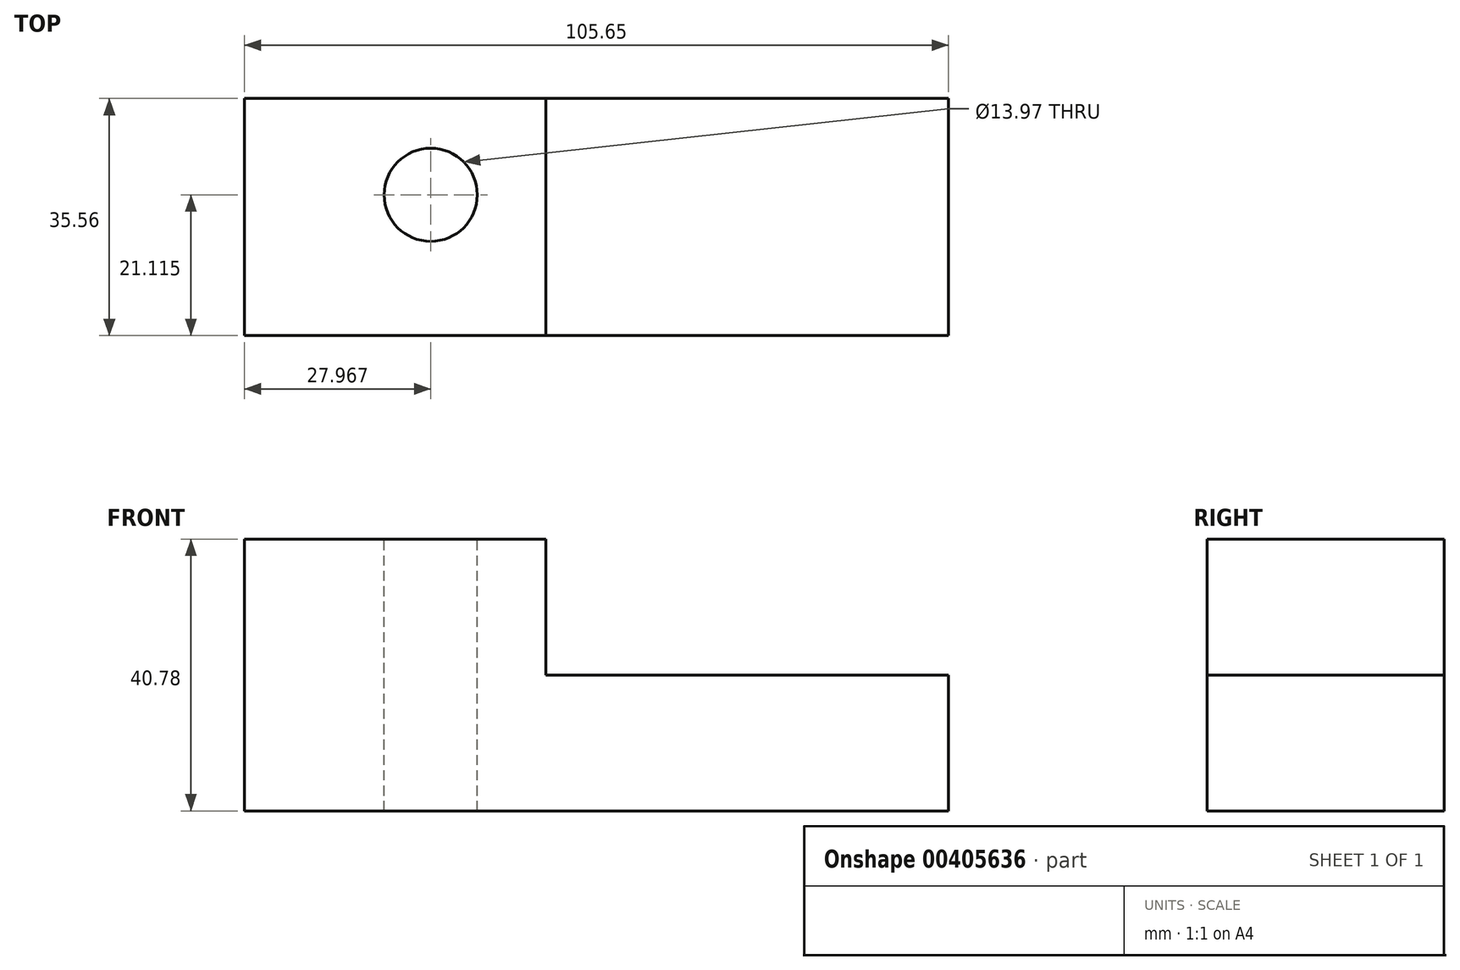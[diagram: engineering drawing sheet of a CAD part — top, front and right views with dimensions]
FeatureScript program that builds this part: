
annotation { "Feature Type Name" : "Feature", "Feature Type Description" : "" }
export const myFeature = defineFeature(function(context is Context, id is Id, definition is map)
    precondition{}
    {
        {
            var Q0;
            Q0=qCreatedBy(makeId("Front.planeOp"),FACE);
            var sketch = newSketch(context, id + "F0", { "sketchPlane" : qUnion([Q0])});
            skLineSegment(sketch, "E0.bottom", {"start": v(0, 0) * mm, "end": v(-45.26, 0) * mm});
            skLineSegment(sketch, "E0.top", {"start": v(0, 40.78) * mm, "end": v(-45.26, 40.78) * mm});
            skLineSegment(sketch, "E0.left", {"start": v(0, 20.39) * mm, "end": v(0, 40.78) * mm});
            skLineSegment(sketch, "E0.right", {"start": v(-45.26, 0) * mm, "end": v(-45.26, 40.78) * mm});
            skPoint(sketch, "E1.oppositeSnap0", {"position": v(-22.63, 0) * mm});
            skLineSegment(sketch, "E1.bottom", {"start": v(0, 20.39) * mm, "end": v(60.4, 20.39) * mm});
            skLineSegment(sketch, "E1.top", {"start": v(0, 0) * mm, "end": v(60.4, 0) * mm});
            skLineSegment(sketch, "E1.right", {"start": v(60.4, 20.39) * mm, "end": v(60.4, 0) * mm});
            skSolve(sketch);
        }
        {
            var Q0;
            Q0=makeQuery(id+"F0.imprint","IMPRINT",FACE,{"disambiguationData":[TD([[makeQuery(id+"F0.imprint","IMPRINT",EDGE,{"derivedFrom":sQuery(id+"F0.wireOp",EDGE,"E0.bottom")}),-1.0]])]});
            extrude(context, id + "F1", {"entities" : qUnion([Q0]), "depth" : 35.56 * mm});
        }
        {
            var Q0;
            Q0=makeQuery(id+"F1.opExtrude","SWEPT_FACE",FACE,{"disambiguationData":[OSD([sQuery(id+"F0.wireOp",EDGE,"E0.top")])]});
            var sketch = newSketch(context, id + "F2", { "sketchPlane" : qUnion([Q0])});
            skCircle(sketch, "E2", {"center": v(-17.3, -14.45) * mm, "radius": 7.82 * mm});
            skSolve(sketch);
        }
        {
            var Q0;
            Q0=sQuery(id+"F2.wireOp",VERTEX,"E2.center");
            var Q1;
            Q1=makeQuery(id+"F1.opExtrude","SWEPT_BODY",BODY,{"disambiguationData":[OSD([sQuery(id+"F0.wireOp",EDGE,"E0.bottom"),sQuery(id+"F0.wireOp",EDGE,"E0.top"),sQuery(id+"F0.wireOp",EDGE,"E0.left"),sQuery(id+"F0.wireOp",EDGE,"E0.right"),sQuery(id+"F0.wireOp",EDGE,"E1.bottom"),sQuery(id+"F0.wireOp",EDGE,"E1.top"),sQuery(id+"F0.wireOp",EDGE,"E1.right")])]});
            hole(context, id + "F3", {"style" : HoleStyle.SIMPLE, "endStyle" : HoleEndStyle.THROUGH, "holeDiameter" : 13.97 * mm, "isTappedThrough" : true, "tappedDepth" : 12.7 * mm, "tapClearance" : 3, "locations" : qUnion([Q0]), "scope" : qUnion([Q1])});
        }
    });
